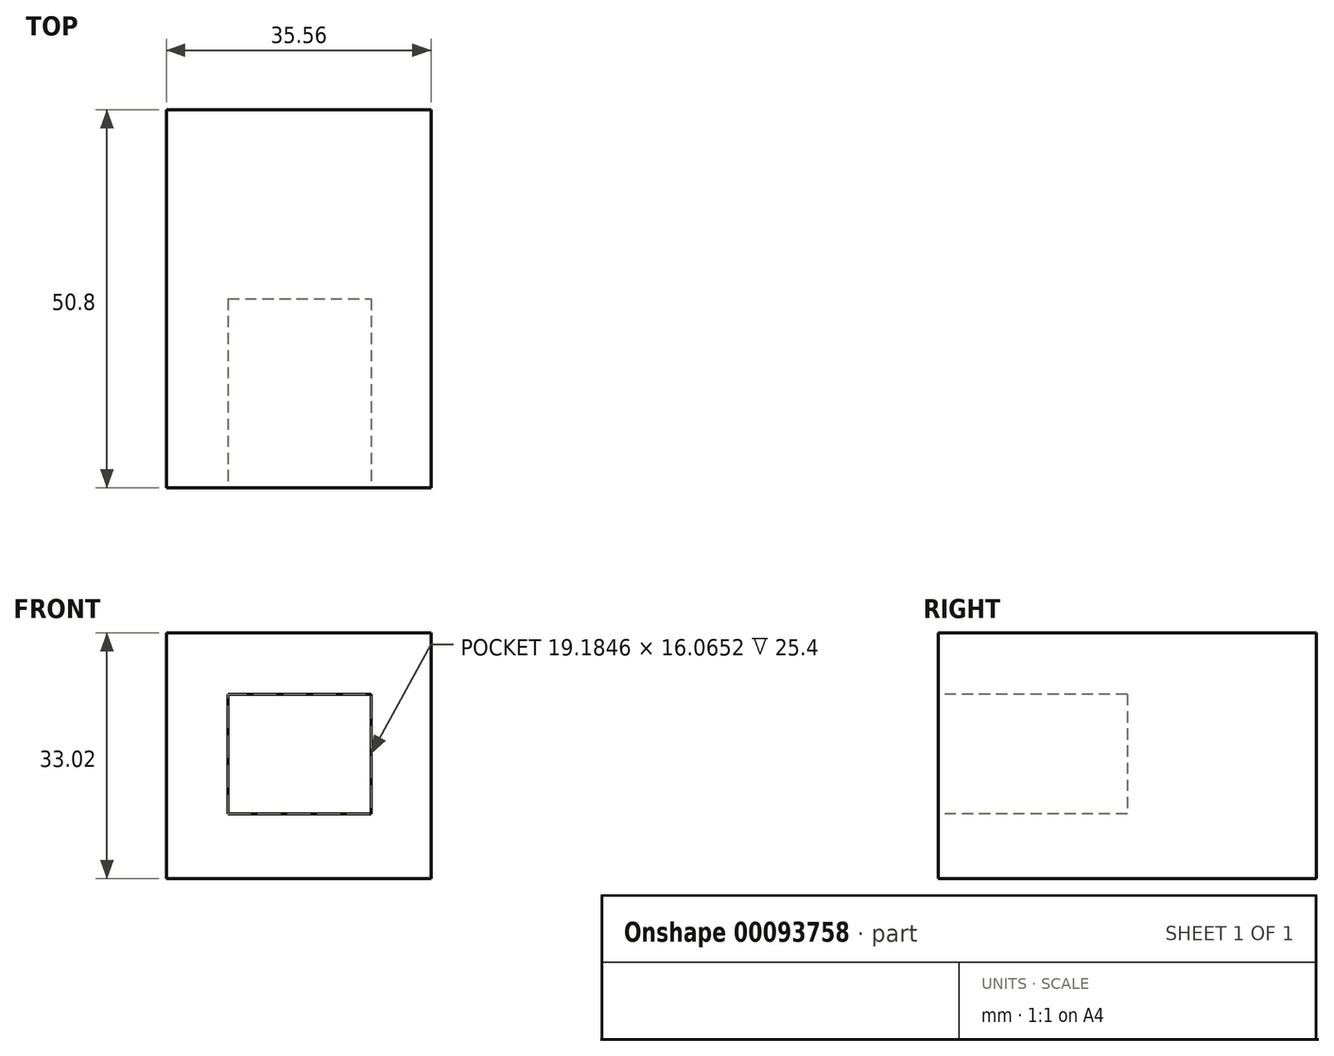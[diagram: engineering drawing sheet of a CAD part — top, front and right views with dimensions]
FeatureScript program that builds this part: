
annotation { "Feature Type Name" : "Feature", "Feature Type Description" : "" }
export const myFeature = defineFeature(function(context is Context, id is Id, definition is map)
    precondition{}
    {
        {
            var Q0;
            Q0=qCreatedBy(makeId("Front.planeOp"),FACE);
            var sketch = newSketch(context, id + "F0", { "sketchPlane" : qUnion([Q0])});
            skLineSegment(sketch, "E0.bottom", {"start": v(0, 0) * mm, "end": v(-35.56, 0) * mm});
            skLineSegment(sketch, "E0.top", {"start": v(0, 33.02) * mm, "end": v(-35.56, 33.02) * mm});
            skLineSegment(sketch, "E0.left", {"start": v(0, 0) * mm, "end": v(0, 33.02) * mm});
            skLineSegment(sketch, "E0.right", {"start": v(-35.56, 0) * mm, "end": v(-35.56, 33.02) * mm});
            skSolve(sketch);
        }
        {
            var Q0;
            Q0 = qSketchRegion(id + "F0", true);
            extrude(context, id + "F1", {"entities" : qUnion([Q0]), "oppositeDirection" : true, "depth" : 50.8 * mm});
        }
        {
            var Q0;
            Q0=makeQuery(id+"F1.opExtrude","CAP_FACE",FACE,{"disambiguationData":[OSD([sQuery(id+"F0.wireOp",EDGE,"E0.bottom"),sQuery(id+"F0.wireOp",EDGE,"E0.top"),sQuery(id+"F0.wireOp",EDGE,"E0.left"),sQuery(id+"F0.wireOp",EDGE,"E0.right")])],"isStart":true});
            var sketch = newSketch(context, id + "F2", { "sketchPlane" : qUnion([Q0])});
            skLineSegment(sketch, "E1.bottom", {"start": v(-27.27, 24.79) * mm, "end": v(-8.08, 24.79) * mm});
            skLineSegment(sketch, "E1.top", {"start": v(-27.27, 8.72) * mm, "end": v(-8.08, 8.72) * mm});
            skLineSegment(sketch, "E1.left", {"start": v(-27.27, 24.79) * mm, "end": v(-27.27, 8.72) * mm});
            skLineSegment(sketch, "E1.right", {"start": v(-8.08, 24.79) * mm, "end": v(-8.08, 8.72) * mm});
            skSolve(sketch);
        }
        {
            var Q0;
            Q0=makeQuery(id+"F2.imprint","IMPRINT",FACE,{"disambiguationData":[TD([[makeQuery(id+"F2.imprint","IMPRINT",EDGE,{"derivedFrom":sQuery(id+"F2.wireOp",EDGE,"E1.bottom")}),-1.0]])]});
            extrude(context, id + "F3", {"entities" : qUnion([Q0]), "operationType" : NewBodyOperationType.REMOVE, "oppositeDirection" : true, "depth" : 25.4 * mm});
        }
    });
